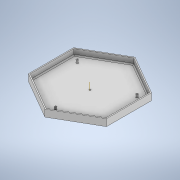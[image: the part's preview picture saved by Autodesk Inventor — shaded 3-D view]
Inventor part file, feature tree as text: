
AUTODESK INVENTOR PART (.ipt)
format: ipt  version: 2020 (Build 240168000, 168)  size: 148,480 bytes
history: native  units: in
note: dims shown in document units (in); Inventor stores cm internally (conversion verified against a paired STEP export)
features: sketch x5, extrude x3, hole x2, other x2, pattern_circular x1, fillet x1
ambient origin geometry x8: Origin, YZ Plane, XZ Plane, XY Plane, X Axis, Y Axis, Z Axis, Center Point
bodies: Solid1 (feature_tree)
feature tree (14):
  extrude  "Extrusion1"  Depth=3.3465in
  extrude  "Extrusion2"  TaperAngle=0.0deg  [1 undecoded]
  extrude  "Extrusion3"  Depth=0.4331in TaperAngle=0.0deg
  hole  "Hole1"  [1 undecoded]
  pattern_circular  "Circular Pattern1"  [2 undecoded]
  fillet  "Fillet1"  [1 undecoded]
  hole  "Hole2"  [1 undecoded]
  sketch  "Sketch1"  dims[d0=0.0in d1=3.3465in]
  sketch  "Sketch2"  dims[d2=0.5118in d3=0.0in d6=0.0in]
  sketch  "Sketch3"  dims[d7=0.0787in d8=0.4331in d9=0.0in]
  sketch  "Sketch4"  dims[d10=0.1575in d11=2.5591in]
  other  "Work Axis1"
  other  "Work Axis2"
  sketch  "Sketch5"  dims[d12=0.1969in d13=0.0in d14=2.5591in d15=0.0in d16=0.0591in d17=0.2362in d18=0.1575in d19=0.0787in d20=90.0deg d21=0.315in d22=0.8108in d23=1.1811in d24=360.0deg d26=0.0787in d27=0.1181in d28=0.2362in d29=0.1575in d30=0.0787in d31=90.0deg d32=0.1181in d33=0.0in]
note: 6 required parameter values undecoded (feature->parameter linkage not recoverable at this tier; creation-order binding heuristic only, values carry confidence <= 0.55)
